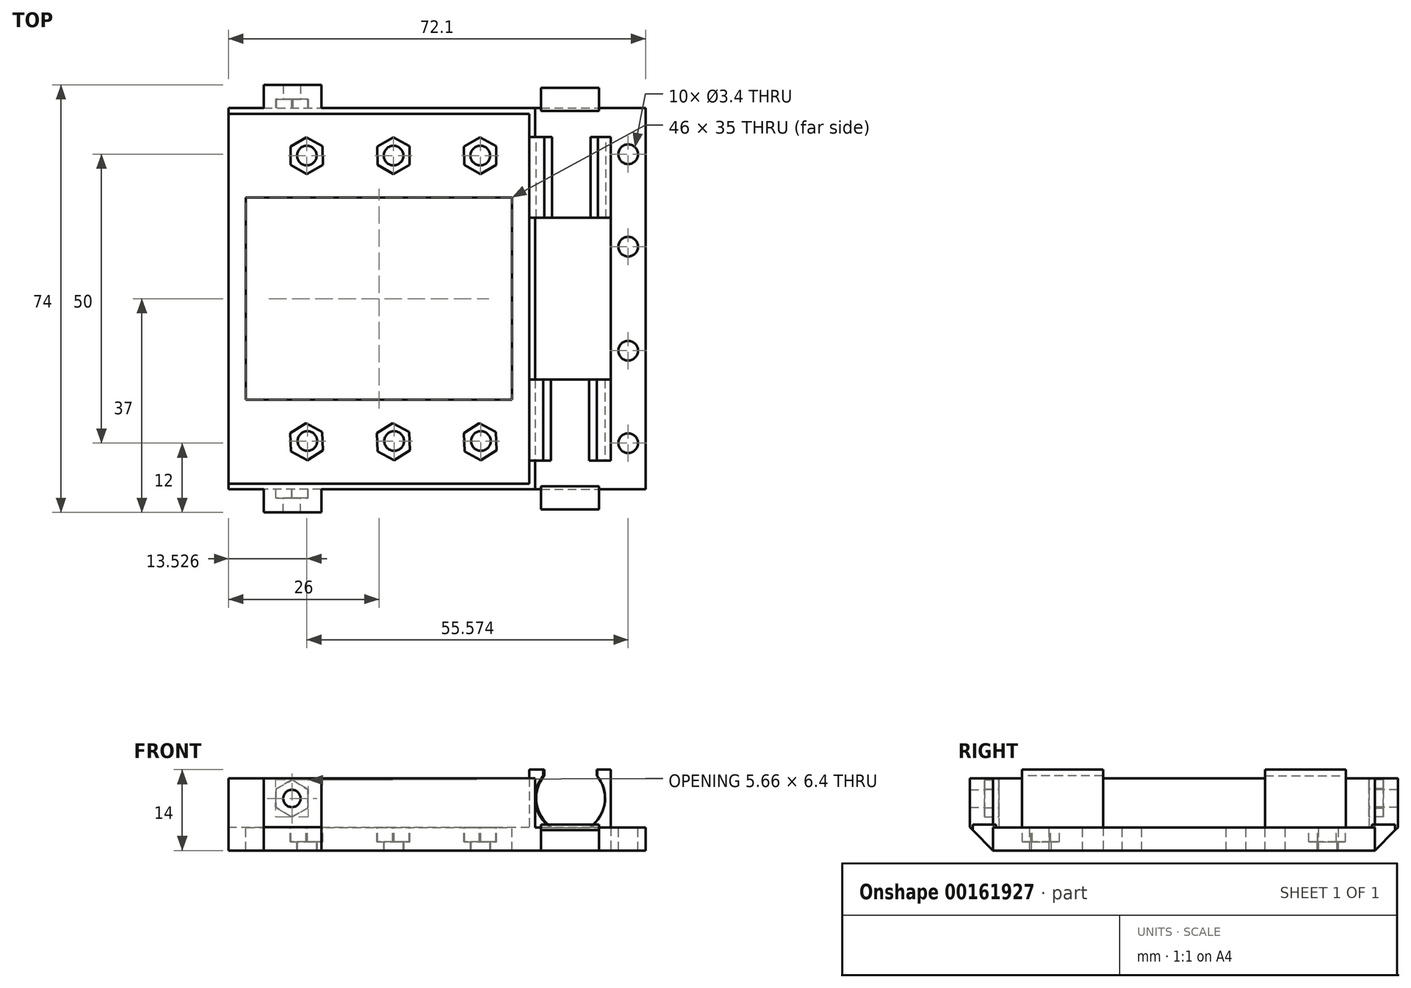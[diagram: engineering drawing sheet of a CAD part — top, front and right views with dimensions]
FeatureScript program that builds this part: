
annotation { "Feature Type Name" : "Feature", "Feature Type Description" : "" }
export const myFeature = defineFeature(function(context is Context, id is Id, definition is map)
    precondition{}
    {
        {
            var Q0;
            Q0=qCreatedBy(makeId("Top.planeOp"),FACE);
            var sketch = newSketch(context, id + "F0", { "sketchPlane" : qUnion([Q0])});
            skLineSegment(sketch, "E0.bottom", {"start": v(-26.5, 33) * mm, "end": v(26.5, 33) * mm});
            skLineSegment(sketch, "E0.top", {"start": v(-26.5, -33) * mm, "end": v(26.5, -33) * mm});
            skLineSegment(sketch, "E0.left", {"start": v(-26.5, 33) * mm, "end": v(-26.5, -33) * mm});
            skLineSegment(sketch, "E0.right", {"start": v(26.5, 33) * mm, "end": v(26.5, -33) * mm});
            skPoint(sketch, "E0.middle", {"position": v(0, 0) * mm});
            skSolve(sketch);
        }
        {
            var Q0;
            Q0 = qSketchRegion(id + "F0", true);
            extrude(context, id + "F1", {"entities" : qUnion([Q0]), "depth" : 12.5 * mm});
        }
        {
            var Q0;
            Q0=makeQuery(id+"F1.opExtrude","SWEPT_FACE",FACE,{"disambiguationData":[OSD([sQuery(id+"F0.wireOp",EDGE,"E0.left")])]});
            var sketch = newSketch(context, id + "F2", { "sketchPlane" : qUnion([Q0])});
            skLineSegment(sketch, "E1.bottom", {"start": v(-32, 12.5) * mm, "end": v(32, 12.5) * mm});
            skLineSegment(sketch, "E1.top", {"start": v(-32, 4) * mm, "end": v(32, 4) * mm});
            skLineSegment(sketch, "E1.left", {"start": v(-32, 12.5) * mm, "end": v(-32, 4) * mm});
            skLineSegment(sketch, "E1.right", {"start": v(32, 12.5) * mm, "end": v(32, 4) * mm});
            skSolve(sketch);
        }
        {
            var Q0;
            Q0 = qSketchRegion(id + "F2", true);
            extrude(context, id + "F3", {"entities" : qUnion([Q0]), "operationType" : NewBodyOperationType.REMOVE, "oppositeDirection" : true, "depth" : 52 * mm});
        }
        {
            var Q0;
            Q0=makeQuery(id+"F3.boolean.opBoolean","COPY",FACE,{"derivedFrom":makeQuery(id+"F3.opExtrude","SWEPT_FACE",FACE,{"disambiguationData":[OSD([sQuery(id+"F2.wireOp",EDGE,"E1.top")])]})});
            var sketch = newSketch(context, id + "F4", { "sketchPlane" : qUnion([Q0])});
            skLineSegment(sketch, "E2.bottom", {"start": v(-23.5, 17.5) * mm, "end": v(22.5, 17.5) * mm});
            skLineSegment(sketch, "E2.top", {"start": v(-23.5, -17.5) * mm, "end": v(22.5, -17.5) * mm});
            skLineSegment(sketch, "E2.left", {"start": v(-23.5, 17.5) * mm, "end": v(-23.5, -17.5) * mm});
            skLineSegment(sketch, "E2.right", {"start": v(22.5, 17.5) * mm, "end": v(22.5, -17.5) * mm});
            skSolve(sketch);
        }
        {
            var Q0;
            Q0 = qSketchRegion(id + "F4", true);
            extrude(context, id + "F5", {"entities" : qUnion([Q0]), "operationType" : NewBodyOperationType.REMOVE, "oppositeDirection" : true, "depth" : 5 * mm});
        }
        {
            var Q0;
            Q0=makeQuery(id+"F1.opExtrude","SWEPT_FACE",FACE,{"disambiguationData":[OSD([sQuery(id+"F0.wireOp",EDGE,"E0.right")])]});
            var sketch = newSketch(context, id + "F6", { "sketchPlane" : qUnion([Q0])});
            skLineSegment(sketch, "E3.bottom", {"start": v(-28, 12.5) * mm, "end": v(-14, 12.5) * mm});
            skLineSegment(sketch, "E3.top", {"start": v(-28, 0) * mm, "end": v(-14, 0) * mm});
            skLineSegment(sketch, "E3.left", {"start": v(-28, 12.5) * mm, "end": v(-28, 0) * mm});
            skLineSegment(sketch, "E3.right", {"start": v(-14, 12.5) * mm, "end": v(-14, 0) * mm});
            skSolve(sketch);
        }
        {
            var Q0;
            Q0 = qSketchRegion(id + "F6", true);
            extrude(context, id + "F7", {"entities" : qUnion([Q0]), "operationType" : NewBodyOperationType.REMOVE, "oppositeDirection" : true, "depth" : 1 * mm});
        }
        {
            var Q0;
            Q0=makeQuery(id+"F7.boolean.opBoolean","COPY",FACE,{"derivedFrom":makeQuery(id+"F7.opExtrude","CAP_FACE",FACE,{"disambiguationData":[OSD([sQuery(id+"F6.wireOp",EDGE,"E3.bottom"),sQuery(id+"F6.wireOp",EDGE,"E3.top"),sQuery(id+"F6.wireOp",EDGE,"E3.left"),sQuery(id+"F6.wireOp",EDGE,"E3.right")])],"isStart":false})});
            var sketch = newSketch(context, id + "F8", { "sketchPlane" : qUnion([Q0])});
            skLineSegment(sketch, "E4.bottom", {"start": v(-14, 0) * mm, "end": v(-28, 0) * mm});
            skLineSegment(sketch, "E4.top", {"start": v(-14, 14) * mm, "end": v(-28, 14) * mm});
            skLineSegment(sketch, "E4.left", {"start": v(-14, 0) * mm, "end": v(-14, 14) * mm});
            skLineSegment(sketch, "E4.right", {"start": v(-28, 0) * mm, "end": v(-28, 14) * mm});
            skSolve(sketch);
        }
        {
            var Q0;
            Q0 = qSketchRegion(id + "F8", true);
            extrude(context, id + "F9", {"entities" : qUnion([Q0]), "operationType" : NewBodyOperationType.ADD, "depth" : 14.1 * mm});
        }
        {
            var Q0;
            Q0=makeQuery(id+"F9.opExtrude","SWEPT_FACE",FACE,{"disambiguationData":[OSD([sQuery(id+"F8.wireOp",EDGE,"E4.right")])]});
            var sketch = newSketch(context, id + "F10", { "sketchPlane" : qUnion([Q0])});
            skArc(sketch, "E5", {"start": v(27.89, 12.91) * mm, "mid": v(26.56, 8.16) * mm, "end": v(29.21, 4) * mm});
            skLineSegment(sketch, "E6", {"start": v(27.89, 14) * mm, "end": v(27.89, 12.91) * mm});
            skLineSegment(sketch, "E7", {"start": v(37.2, 12.91) * mm, "end": v(37.2, 14) * mm});
            skLineSegment(sketch, "E8", {"start": v(27.89, 14) * mm, "end": v(37.2, 14) * mm});
            skLineSegment(sketch, "E9", {"start": v(29.21, 4) * mm, "end": v(35.88, 4) * mm});
            skArc(sketch, "E10.trimOffspring", {"start": v(35.88, 4) * mm, "mid": v(38.53, 8.16) * mm, "end": v(37.2, 12.91) * mm});
            skSolve(sketch);
        }
        {
            var Q0;
            Q0 = qSketchRegion(id + "F10", true);
            extrude(context, id + "F11", {"entities" : qUnion([Q0]), "operationType" : NewBodyOperationType.REMOVE, "oppositeDirection" : true, "depth" : 14 * mm});
        }
        {
            var Q0;
            {var subQ0=sQuery(id+"F0.wireOp",EDGE,"E0.bottom");var subQ1=sQuery(id+"F0.wireOp",EDGE,"E0.right");Q0=makeQuery(id+"F7.boolean.opBoolean","SPLIT",FACE,{"disambiguationData":[TD([makeQuery(id+"F1.opExtrude","SWEPT_FACE",FACE,{"disambiguationData":[OSD([subQ0])]})])],"derivedFrom":makeQuery(id+"F1.opExtrude","SWEPT_FACE",FACE,{"disambiguationData":[OSD([subQ1])]})});}
            var sketch = newSketch(context, id + "F12", { "sketchPlane" : qUnion([Q0])});
            skLineSegment(sketch, "E11.bottom", {"start": v(28, 0) * mm, "end": v(14, 0) * mm});
            skLineSegment(sketch, "E11.top", {"start": v(28, 14) * mm, "end": v(14, 14) * mm});
            skLineSegment(sketch, "E11.left", {"start": v(28, 0) * mm, "end": v(28, 14) * mm});
            skLineSegment(sketch, "E11.right", {"start": v(14, 0) * mm, "end": v(14, 14) * mm});
            skSolve(sketch);
        }
        {
            var Q0;
            Q0 = qSketchRegion(id + "F12", true);
            var Q1;
            {var subQ3=sQuery(id+"F2.wireOp",EDGE,"E1.right");var subQ4=sQuery(id+"F2.wireOp",EDGE,"E1.top");var subQ7=sQuery(id+"F2.wireOp",EDGE,"E1.left");var subQ8=makeQuery(id+"F3.boolean.opBoolean","COPY",FACE,{"derivedFrom":makeQuery(id+"F3.opExtrude","CAP_FACE",FACE,{"disambiguationData":[OSD([sQuery(id+"F2.wireOp",EDGE,"E1.bottom"),subQ4,subQ7,subQ3])],"isStart":false})});Q1=makeQuery(id+"F9.boolean.opBoolean","MERGE",FACE,{"derivedFrom":[makeQuery(id+"F7.boolean.opBoolean","SPLIT",FACE,{"disambiguationData":[TD([makeQuery(id+"F3.boolean.opBoolean","COPY",FACE,{"derivedFrom":makeQuery(id+"F3.opExtrude","SWEPT_FACE",FACE,{"disambiguationData":[OSD([subQ7])]})})])],"derivedFrom":subQ8}),makeQuery(id+"F7.boolean.opBoolean","SPLIT",FACE,{"disambiguationData":[TD([makeQuery(id+"F3.boolean.opBoolean","COPY",FACE,{"derivedFrom":makeQuery(id+"F3.opExtrude","SWEPT_FACE",FACE,{"disambiguationData":[OSD([subQ3])]})})])],"derivedFrom":subQ8}),makeQuery(id+"F9.opExtrude","CAP_FACE",FACE,{"disambiguationData":[OSD([sQuery(id+"F8.wireOp",EDGE,"E4.bottom"),sQuery(id+"F8.wireOp",EDGE,"E4.top"),sQuery(id+"F8.wireOp",EDGE,"E4.left"),sQuery(id+"F8.wireOp",EDGE,"E4.right")])],"isStart":true})]});}
            extrude(context, id + "F13", {"entities" : qUnion([Q0]), "operationType" : NewBodyOperationType.ADD, "endBound" : BoundingType.UP_TO_SURFACE, "oppositeDirection" : true, "endBoundEntityFace" : qUnion([Q1]), "depth" : 25 * mm, "hasSecondDirection" : true, "secondDirectionOppositeDirection" : false, "secondDirectionDepth" : 13.1 * mm});
        }
        {
            var Q0;
            Q0=makeQuery(id+"F13.opExtrude","SWEPT_FACE",FACE,{"disambiguationData":[OSD([sQuery(id+"F12.wireOp",EDGE,"E11.left")])]});
            var sketch = newSketch(context, id + "F14", { "sketchPlane" : qUnion([Q0])});
            skArc(sketch, "E12", {"start": v(-37.37, 12.94) * mm, "mid": v(-38.72, 8.18) * mm, "end": v(-36.07, 4) * mm});
            skLineSegment(sketch, "E13", {"start": v(-36.07, 4) * mm, "end": v(-29.4, 4) * mm});
            skLineSegment(sketch, "E14", {"start": v(-37.37, 14) * mm, "end": v(-37.37, 12.94) * mm});
            skLineSegment(sketch, "E15", {"start": v(-28.1, 12.94) * mm, "end": v(-28.1, 14) * mm});
            skArc(sketch, "E16.trimOffspring", {"start": v(-29.4, 4) * mm, "mid": v(-26.75, 8.18) * mm, "end": v(-28.1, 12.94) * mm});
            skLineSegment(sketch, "E17", {"start": v(-37.37, 14) * mm, "end": v(-28.1, 14) * mm});
            skSolve(sketch);
        }
        {
            var Q0;
            Q0 = qSketchRegion(id + "F14", true);
            extrude(context, id + "F15", {"entities" : qUnion([Q0]), "operationType" : NewBodyOperationType.REMOVE, "oppositeDirection" : true, "depth" : 14 * mm});
        }
        {
            var Q0;
            {var subQ0=sQuery(id+"F0.wireOp",EDGE,"E0.right");var subQ2=sQuery(id+"F0.wireOp",EDGE,"E0.top");Q0=makeQuery(id+"F7.boolean.opBoolean","SPLIT",FACE,{"disambiguationData":[TD([makeQuery(id+"F1.opExtrude","SWEPT_FACE",FACE,{"disambiguationData":[OSD([subQ2])]})])],"derivedFrom":makeQuery(id+"F1.opExtrude","SWEPT_FACE",FACE,{"disambiguationData":[OSD([subQ0])]})});}
            var sketch = newSketch(context, id + "F16", { "sketchPlane" : qUnion([Q0])});
            skLineSegment(sketch, "E18.bottom", {"start": v(-33, 4) * mm, "end": v(-28, 4) * mm});
            skLineSegment(sketch, "E18.top", {"start": v(-33, 0) * mm, "end": v(-28, 0) * mm});
            skLineSegment(sketch, "E18.left", {"start": v(-33, 4) * mm, "end": v(-33, 0) * mm});
            skLineSegment(sketch, "E18.right", {"start": v(-28, 4) * mm, "end": v(-28, 0) * mm});
            skSolve(sketch);
        }
        {
            var Q0;
            Q0 = qSketchRegion(id + "F16", true);
            var Q1;
            Q1=makeQuery(id+"F9.opExtrude","CAP_FACE",FACE,{"disambiguationData":[OSD([sQuery(id+"F8.wireOp",EDGE,"E4.bottom"),sQuery(id+"F8.wireOp",EDGE,"E4.top"),sQuery(id+"F8.wireOp",EDGE,"E4.left"),sQuery(id+"F8.wireOp",EDGE,"E4.right")])],"isStart":false});
            extrude(context, id + "F17", {"entities" : qUnion([Q0]), "operationType" : NewBodyOperationType.ADD, "endBound" : BoundingType.UP_TO_SURFACE, "endBoundEntityFace" : qUnion([Q1]), "depth" : 25 * mm});
        }
        {
            var Q0;
            {var subQ0=sQuery(id+"F0.wireOp",EDGE,"E0.right");var subQ3=sQuery(id+"F0.wireOp",EDGE,"E0.bottom");var subQ6=makeQuery(id+"F1.opExtrude","SWEPT_FACE",FACE,{"disambiguationData":[OSD([subQ3])]});Q0=makeQuery(id+"F13.boolean.opBoolean","SPLIT",FACE,{"disambiguationData":[TD([subQ6])],"derivedFrom":makeQuery(id+"F7.boolean.opBoolean","SPLIT",FACE,{"disambiguationData":[TD([subQ6])],"derivedFrom":makeQuery(id+"F1.opExtrude","SWEPT_FACE",FACE,{"disambiguationData":[OSD([subQ0])]})})});}
            var sketch = newSketch(context, id + "F18", { "sketchPlane" : qUnion([Q0])});
            skLineSegment(sketch, "E19.bottom", {"start": v(28, 4) * mm, "end": v(33, 4) * mm});
            skLineSegment(sketch, "E19.top", {"start": v(28, 0) * mm, "end": v(33, 0) * mm});
            skLineSegment(sketch, "E19.left", {"start": v(28, 4) * mm, "end": v(28, 0) * mm});
            skLineSegment(sketch, "E19.right", {"start": v(33, 4) * mm, "end": v(33, 0) * mm});
            skSolve(sketch);
        }
        {
            var Q0;
            Q0 = qSketchRegion(id + "F18", true);
            var Q1;
            Q1=makeQuery(id+"F13.opExtrude","CAP_FACE",FACE,{"disambiguationData":[OSD([sQuery(id+"F12.wireOp",EDGE,"E11.bottom"),sQuery(id+"F12.wireOp",EDGE,"E11.top"),sQuery(id+"F12.wireOp",EDGE,"E11.left"),sQuery(id+"F12.wireOp",EDGE,"E11.right")])],"isStart":true});
            extrude(context, id + "F19", {"entities" : qUnion([Q0]), "operationType" : NewBodyOperationType.ADD, "endBound" : BoundingType.UP_TO_SURFACE, "endBoundEntityFace" : qUnion([Q1]), "depth" : 25 * mm});
        }
        {
            var Q0;
            {var subQ0=sQuery(id+"F8.wireOp",EDGE,"E4.right");var subQ1=sQuery(id+"F8.wireOp",EDGE,"E4.left");var subQ2=sQuery(id+"F8.wireOp",EDGE,"E4.top");var subQ3=sQuery(id+"F8.wireOp",EDGE,"E4.bottom");Q0=makeQuery(id+"F17.boolean.opBoolean","MERGE",FACE,{"derivedFrom":[makeQuery(id+"F9.opExtrude","CAP_FACE",FACE,{"disambiguationData":[OSD([subQ3,subQ2,subQ1,subQ0])],"isStart":false}),makeQuery(id+"F17.opExtrude","CAP_FACE",FACE,{"disambiguationData":[OSD([subQ3,subQ2,subQ1,subQ0])],"isStart":false})]});}
            var sketch = newSketch(context, id + "F20", { "sketchPlane" : qUnion([Q0])});
            skLineSegment(sketch, "E20.bottom", {"start": v(-33, 4) * mm, "end": v(33, 4) * mm});
            skLineSegment(sketch, "E20.top", {"start": v(-33, 0) * mm, "end": v(33, 0) * mm});
            skLineSegment(sketch, "E20.left", {"start": v(-33, 4) * mm, "end": v(-33, 0) * mm});
            skLineSegment(sketch, "E20.right", {"start": v(33, 4) * mm, "end": v(33, 0) * mm});
            skSolve(sketch);
        }
        {
            var Q0;
            Q0 = qSketchRegion(id + "F20", true);
            extrude(context, id + "F21", {"entities" : qUnion([Q0]), "operationType" : NewBodyOperationType.ADD, "depth" : 6 * mm});
        }
        {
            var Q0;
            Q0=makeQuery(id+"F21.boolean.opBoolean","MERGE",FACE,{"derivedFrom":[makeQuery(id+"F17.boolean.opBoolean","MERGE",FACE,{"derivedFrom":[makeQuery(id+"F1.opExtrude","SWEPT_FACE",FACE,{"disambiguationData":[OSD([sQuery(id+"F0.wireOp",EDGE,"E0.top")])]}),makeQuery(id+"F17.opExtrude","SWEPT_FACE",FACE,{"disambiguationData":[OSD([sQuery(id+"F16.wireOp",EDGE,"E18.left")])]})]}),makeQuery(id+"F21.opExtrude","SWEPT_FACE",FACE,{"disambiguationData":[OSD([sQuery(id+"F20.wireOp",EDGE,"E20.left")])]})]});
            var sketch = newSketch(context, id + "F22", { "sketchPlane" : qUnion([Q0])});
            skLineSegment(sketch, "E21.bottom", {"start": v(37.55, 0) * mm, "end": v(27.55, 0) * mm});
            skLineSegment(sketch, "E21.top", {"start": v(37.55, 4.5) * mm, "end": v(27.55, 4.5) * mm});
            skLineSegment(sketch, "E21.left", {"start": v(37.55, 0) * mm, "end": v(37.55, 4.5) * mm});
            skLineSegment(sketch, "E21.right", {"start": v(27.55, 0) * mm, "end": v(27.55, 4.5) * mm});
            skSolve(sketch);
        }
        {
            var Q0;
            Q0 = qSketchRegion(id + "F22", true);
            extrude(context, id + "F23", {"entities" : qUnion([Q0]), "operationType" : NewBodyOperationType.ADD, "oppositeDirection" : true, "depth" : .5 * mm, "hasSecondDirection" : true, "secondDirectionOppositeDirection" : false, "secondDirectionDepth" : 3.5 * mm});
        }
        {
            var Q0;
            Q0=makeQuery(id+"F23.opExtrude","SWEPT_FACE",FACE,{"disambiguationData":[OSD([sQuery(id+"F22.wireOp",EDGE,"E21.left")])]});
            var sketch = newSketch(context, id + "F24", { "sketchPlane" : qUnion([Q0])});
            skLineSegment(sketch, "E22", {"start": v(-33, 0) * mm, "end": v(-36.5, 3.5) * mm});
            skLineSegment(sketch, "E23", {"start": v(-36.5, 3.5) * mm, "end": v(-36.5, 0) * mm});
            skLineSegment(sketch, "E24", {"start": v(-36.5, 0) * mm, "end": v(-33, 0) * mm});
            skSolve(sketch);
        }
        {
            var Q0;
            Q0 = qSketchRegion(id + "F24", true);
            extrude(context, id + "F25", {"entities" : qUnion([Q0]), "operationType" : NewBodyOperationType.REMOVE, "oppositeDirection" : true, "depth" : 10 * mm});
        }
        {
            var Q0;
            {var subQ1=sQuery(id+"F0.wireOp",EDGE,"E0.left");var subQ2=sQuery(id+"F0.wireOp",EDGE,"E0.top");Q0=makeQuery(id+"F23.boolean.opBoolean","SPLIT",FACE,{"disambiguationData":[TD([makeQuery(id+"F1.opExtrude","SWEPT_FACE",FACE,{"disambiguationData":[OSD([subQ1])]})])],"derivedFrom":makeQuery(id+"F21.boolean.opBoolean","MERGE",FACE,{"derivedFrom":[makeQuery(id+"F17.boolean.opBoolean","MERGE",FACE,{"derivedFrom":[makeQuery(id+"F1.opExtrude","SWEPT_FACE",FACE,{"disambiguationData":[OSD([subQ2])]}),makeQuery(id+"F17.opExtrude","SWEPT_FACE",FACE,{"disambiguationData":[OSD([sQuery(id+"F16.wireOp",EDGE,"E18.left")])]})]}),makeQuery(id+"F21.opExtrude","SWEPT_FACE",FACE,{"disambiguationData":[OSD([sQuery(id+"F20.wireOp",EDGE,"E20.left")])]})]})});}
            var sketch = newSketch(context, id + "F26", { "sketchPlane" : qUnion([Q0])});
            skLineSegment(sketch, "E25.bottom", {"start": v(-20.45, 12.5) * mm, "end": v(-10.45, 12.5) * mm});
            skLineSegment(sketch, "E25.top", {"start": v(-20.45, 0) * mm, "end": v(-10.45, 0) * mm});
            skLineSegment(sketch, "E25.left", {"start": v(-20.45, 12.5) * mm, "end": v(-20.45, 0) * mm});
            skLineSegment(sketch, "E25.right", {"start": v(-10.45, 12.5) * mm, "end": v(-10.45, 0) * mm});
            skSolve(sketch);
        }
        {
            var Q0;
            Q0 = qSketchRegion(id + "F26", true);
            extrude(context, id + "F27", {"entities" : qUnion([Q0]), "operationType" : NewBodyOperationType.ADD, "depth" : 4 * mm});
        }
        {
            var Q0;
            Q0=makeQuery(id+"F27.opExtrude","SWEPT_FACE",FACE,{"disambiguationData":[OSD([sQuery(id+"F26.wireOp",EDGE,"E25.left")])]});
            var sketch = newSketch(context, id + "F28", { "sketchPlane" : qUnion([Q0])});
            skLineSegment(sketch, "E26", {"start": v(37, 0) * mm, "end": v(37, 4.04) * mm});
            skLineSegment(sketch, "E27", {"start": v(37, 4.04) * mm, "end": v(33, 0) * mm});
            skLineSegment(sketch, "E28", {"start": v(33, 0) * mm, "end": v(37, 0) * mm});
            skSolve(sketch);
        }
        {
            var Q0;
            Q0 = qSketchRegion(id + "F28", true);
            var Q1;
            Q1=makeQuery(id+"F27.opExtrude","SWEPT_FACE",FACE,{"disambiguationData":[OSD([sQuery(id+"F26.wireOp",EDGE,"E25.right")])]});
            extrude(context, id + "F29", {"entities" : qUnion([Q0]), "operationType" : NewBodyOperationType.REMOVE, "endBound" : BoundingType.UP_TO_SURFACE, "oppositeDirection" : true, "endBoundEntityFace" : qUnion([Q1]), "depth" : 25 * mm});
        }
        {
            var Q0;
            Q0=makeQuery(id+"F21.boolean.opBoolean","MERGE",FACE,{"derivedFrom":[makeQuery(id+"F19.boolean.opBoolean","MERGE",FACE,{"derivedFrom":[makeQuery(id+"F1.opExtrude","SWEPT_FACE",FACE,{"disambiguationData":[OSD([sQuery(id+"F0.wireOp",EDGE,"E0.bottom")])]}),makeQuery(id+"F19.opExtrude","SWEPT_FACE",FACE,{"disambiguationData":[OSD([sQuery(id+"F18.wireOp",EDGE,"E19.right")])]})]}),makeQuery(id+"F21.opExtrude","SWEPT_FACE",FACE,{"disambiguationData":[OSD([sQuery(id+"F20.wireOp",EDGE,"E20.right")])]})]});
            var sketch = newSketch(context, id + "F30", { "sketchPlane" : qUnion([Q0])});
            skLineSegment(sketch, "E29.bottom", {"start": v(-27.55, 0) * mm, "end": v(-37.55, 0) * mm});
            skLineSegment(sketch, "E29.top", {"start": v(-27.55, 4.5) * mm, "end": v(-37.55, 4.5) * mm});
            skLineSegment(sketch, "E29.left", {"start": v(-27.55, 0) * mm, "end": v(-27.55, 4.5) * mm});
            skLineSegment(sketch, "E29.right", {"start": v(-37.55, 0) * mm, "end": v(-37.55, 4.5) * mm});
            skSolve(sketch);
        }
        {
            var Q0;
            Q0 = qSketchRegion(id + "F30", true);
            extrude(context, id + "F31", {"entities" : qUnion([Q0]), "operationType" : NewBodyOperationType.ADD, "oppositeDirection" : true, "depth" : 0.5 * mm, "hasSecondDirection" : true, "secondDirectionOppositeDirection" : false, "secondDirectionDepth" : 3.5 * mm});
        }
        {
            var Q0;
            Q0=makeQuery(id+"F31.opExtrude","SWEPT_FACE",FACE,{"disambiguationData":[OSD([sQuery(id+"F30.wireOp",EDGE,"E29.right")])]});
            var sketch = newSketch(context, id + "F32", { "sketchPlane" : qUnion([Q0])});
            skLineSegment(sketch, "E30", {"start": v(33, 0) * mm, "end": v(36.5, 3.5) * mm});
            skLineSegment(sketch, "E31", {"start": v(36.5, 3.5) * mm, "end": v(36.5, 0) * mm});
            skLineSegment(sketch, "E32", {"start": v(36.5, 0) * mm, "end": v(33, 0) * mm});
            skSolve(sketch);
        }
        {
            var Q0;
            Q0 = qSketchRegion(id + "F32", true);
            var Q1;
            Q1=makeQuery(id+"F31.opExtrude","SWEPT_FACE",FACE,{"disambiguationData":[OSD([sQuery(id+"F30.wireOp",EDGE,"E29.left")])]});
            extrude(context, id + "F33", {"entities" : qUnion([Q0]), "operationType" : NewBodyOperationType.REMOVE, "endBound" : BoundingType.UP_TO_SURFACE, "oppositeDirection" : true, "endBoundEntityFace" : qUnion([Q1]), "depth" : 25 * mm});
        }
        {
            var Q0;
            {var subQ1=sQuery(id+"F0.wireOp",EDGE,"E0.left");var subQ3=sQuery(id+"F0.wireOp",EDGE,"E0.bottom");Q0=makeQuery(id+"F31.boolean.opBoolean","SPLIT",FACE,{"disambiguationData":[TD([makeQuery(id+"F1.opExtrude","SWEPT_FACE",FACE,{"disambiguationData":[OSD([subQ1])]})])],"derivedFrom":makeQuery(id+"F21.boolean.opBoolean","MERGE",FACE,{"derivedFrom":[makeQuery(id+"F19.boolean.opBoolean","MERGE",FACE,{"derivedFrom":[makeQuery(id+"F1.opExtrude","SWEPT_FACE",FACE,{"disambiguationData":[OSD([subQ3])]}),makeQuery(id+"F19.opExtrude","SWEPT_FACE",FACE,{"disambiguationData":[OSD([sQuery(id+"F18.wireOp",EDGE,"E19.right")])]})]}),makeQuery(id+"F21.opExtrude","SWEPT_FACE",FACE,{"disambiguationData":[OSD([sQuery(id+"F20.wireOp",EDGE,"E20.right")])]})]})});}
            var sketch = newSketch(context, id + "F34", { "sketchPlane" : qUnion([Q0])});
            skLineSegment(sketch, "E33.bottom", {"start": v(10.45, 12.5) * mm, "end": v(20.45, 12.5) * mm});
            skLineSegment(sketch, "E33.top", {"start": v(10.45, 0) * mm, "end": v(20.45, 0) * mm});
            skLineSegment(sketch, "E33.left", {"start": v(10.45, 12.5) * mm, "end": v(10.45, 0) * mm});
            skLineSegment(sketch, "E33.right", {"start": v(20.45, 12.5) * mm, "end": v(20.45, 0) * mm});
            skSolve(sketch);
        }
        {
            var Q0;
            Q0 = qSketchRegion(id + "F34", true);
            extrude(context, id + "F35", {"entities" : qUnion([Q0]), "operationType" : NewBodyOperationType.ADD, "depth" : 4 * mm});
        }
        {
            var Q0;
            Q0=makeQuery(id+"F35.opExtrude","SWEPT_FACE",FACE,{"disambiguationData":[OSD([sQuery(id+"F34.wireOp",EDGE,"E33.left")])]});
            var sketch = newSketch(context, id + "F36", { "sketchPlane" : qUnion([Q0])});
            skLineSegment(sketch, "E34", {"start": v(33, 0) * mm, "end": v(37, 4) * mm});
            skLineSegment(sketch, "E35", {"start": v(37, 4) * mm, "end": v(37, 0) * mm});
            skLineSegment(sketch, "E36", {"start": v(37, 0) * mm, "end": v(33, 0) * mm});
            skSolve(sketch);
        }
        {
            var Q0;
            Q0 = qSketchRegion(id + "F36", true);
            var Q1;
            Q1=makeQuery(id+"F35.opExtrude","SWEPT_FACE",FACE,{"disambiguationData":[OSD([sQuery(id+"F34.wireOp",EDGE,"E33.right")])]});
            extrude(context, id + "F37", {"entities" : qUnion([Q0]), "operationType" : NewBodyOperationType.REMOVE, "endBound" : BoundingType.UP_TO_SURFACE, "oppositeDirection" : true, "endBoundEntityFace" : qUnion([Q1]), "depth" : 25 * mm});
        }
        {
            var Q0;
            Q0=makeQuery(id+"F3.boolean.opBoolean","COPY",FACE,{"derivedFrom":makeQuery(id+"F3.opExtrude","SWEPT_FACE",FACE,{"disambiguationData":[OSD([sQuery(id+"F2.wireOp",EDGE,"E1.right")])]})});
            var sketch = newSketch(context, id + "F38", { "sketchPlane" : qUnion([Q0])});
            skCircle(sketch, "E37.cCircle", {"center": v(15.55, 9) * mm, "radius": 2.77 * mm, "construction": true});
            skLineSegment(sketch, "E37.0", {"start": v(12.8, 10.62) * mm, "end": v(15.57, 12.2) * mm});
            skLineSegment(sketch, "E37.1", {"start": v(15.57, 12.2) * mm, "end": v(18.33, 10.58) * mm});
            skLineSegment(sketch, "E37.2", {"start": v(18.33, 10.58) * mm, "end": v(18.3, 7.38) * mm});
            skLineSegment(sketch, "E37.3", {"start": v(18.3, 7.38) * mm, "end": v(15.53, 5.8) * mm});
            skLineSegment(sketch, "E37.4", {"start": v(15.53, 5.8) * mm, "end": v(12.77, 7.42) * mm});
            skLineSegment(sketch, "E37.5", {"start": v(12.77, 7.42) * mm, "end": v(12.8, 10.62) * mm});
            skPoint(sketch, "E37.0.midPoint", {"position": v(14.18, 11.41) * mm});
            skSolve(sketch);
        }
        {
            var Q0;
            Q0 = qSketchRegion(id + "F38", true);
            extrude(context, id + "F39", {"entities" : qUnion([Q0]), "operationType" : NewBodyOperationType.REMOVE, "oppositeDirection" : true, "depth" : 2.5 * mm});
        }
        {
            var Q0;
            Q0=makeQuery(id+"F3.boolean.opBoolean","COPY",FACE,{"derivedFrom":makeQuery(id+"F3.opExtrude","SWEPT_FACE",FACE,{"disambiguationData":[OSD([sQuery(id+"F2.wireOp",EDGE,"E1.right")])]})});
            var sketch = newSketch(context, id + "F40", { "sketchPlane" : qUnion([Q0])});
            skCircle(sketch, "E38", {"center": v(15.55, 9) * mm, "radius": 1.5 * mm});
            skSolve(sketch);
        }
        {
            var Q0;
            Q0 = qSketchRegion(id + "F40", true);
            extrude(context, id + "F41", {"entities" : qUnion([Q0]), "operationType" : NewBodyOperationType.REMOVE, "oppositeDirection" : true, "depth" : 6 * mm});
        }
        {
            var Q0;
            Q0=makeQuery(id+"F3.boolean.opBoolean","COPY",FACE,{"derivedFrom":makeQuery(id+"F3.opExtrude","SWEPT_FACE",FACE,{"disambiguationData":[OSD([sQuery(id+"F2.wireOp",EDGE,"E1.left")])]})});
            var sketch = newSketch(context, id + "F42", { "sketchPlane" : qUnion([Q0])});
            skCircle(sketch, "E39.cCircle", {"center": v(-15.55, 9) * mm, "radius": 2.77 * mm, "construction": true});
            skLineSegment(sketch, "E39.0", {"start": v(-12.84, 7.3) * mm, "end": v(-15.67, 5.8) * mm});
            skLineSegment(sketch, "E39.1", {"start": v(-15.67, 5.8) * mm, "end": v(-18.38, 7.5) * mm});
            skLineSegment(sketch, "E39.2", {"start": v(-18.38, 7.5) * mm, "end": v(-18.26, 10.7) * mm});
            skLineSegment(sketch, "E39.3", {"start": v(-18.26, 10.7) * mm, "end": v(-15.43, 12.2) * mm});
            skLineSegment(sketch, "E39.4", {"start": v(-15.43, 12.2) * mm, "end": v(-12.72, 10.5) * mm});
            skLineSegment(sketch, "E39.5", {"start": v(-12.72, 10.5) * mm, "end": v(-12.84, 7.3) * mm});
            skPoint(sketch, "E39.0.midPoint", {"position": v(-14.25, 6.55) * mm});
            skSolve(sketch);
        }
        {
            var Q0;
            Q0 = qSketchRegion(id + "F42", true);
            extrude(context, id + "F43", {"entities" : qUnion([Q0]), "operationType" : NewBodyOperationType.REMOVE, "oppositeDirection" : true, "depth" : 2.5 * mm});
        }
        {
            var Q0;
            Q0=makeQuery(id+"F3.boolean.opBoolean","COPY",FACE,{"derivedFrom":makeQuery(id+"F3.opExtrude","SWEPT_FACE",FACE,{"disambiguationData":[OSD([sQuery(id+"F2.wireOp",EDGE,"E1.left")])]})});
            var sketch = newSketch(context, id + "F44", { "sketchPlane" : qUnion([Q0])});
            skCircle(sketch, "E40", {"center": v(-15.55, 9) * mm, "radius": 1.5 * mm});
            skSolve(sketch);
        }
        {
            var Q0;
            Q0 = qSketchRegion(id + "F44", true);
            extrude(context, id + "F45", {"entities" : qUnion([Q0]), "operationType" : NewBodyOperationType.REMOVE, "oppositeDirection" : true, "depth" : 6 * mm});
        }
        {
            var Q0;
            Q0=makeQuery(id+"F21.boolean.opBoolean","MERGE",FACE,{"derivedFrom":[makeQuery(id+"F17.boolean.opBoolean","MERGE",FACE,{"derivedFrom":[makeQuery(id+"F11.boolean.opBoolean","COPY",FACE,{"derivedFrom":makeQuery(id+"F11.opExtrude","SWEPT_FACE",FACE,{"disambiguationData":[OSD([sQuery(id+"F10.wireOp",EDGE,"E9")])]})}),makeQuery(id+"F17.opExtrude","SWEPT_FACE",FACE,{"disambiguationData":[OSD([sQuery(id+"F16.wireOp",EDGE,"E18.bottom")])]})]}),makeQuery(id+"F19.boolean.opBoolean","MERGE",FACE,{"derivedFrom":[makeQuery(id+"F15.boolean.opBoolean","COPY",FACE,{"derivedFrom":makeQuery(id+"F15.opExtrude","SWEPT_FACE",FACE,{"disambiguationData":[OSD([sQuery(id+"F14.wireOp",EDGE,"E13")])]})}),makeQuery(id+"F19.opExtrude","SWEPT_FACE",FACE,{"disambiguationData":[OSD([sQuery(id+"F18.wireOp",EDGE,"E19.bottom")])]})]}),makeQuery(id+"F21.opExtrude","SWEPT_FACE",FACE,{"disambiguationData":[OSD([sQuery(id+"F20.wireOp",EDGE,"E20.bottom")])]})]});
            var sketch = newSketch(context, id + "F46", { "sketchPlane" : qUnion([Q0])});
            skCircle(sketch, "E41", {"center": v(42.6, -25) * mm, "radius": 1.7 * mm});
            skCircle(sketch, "E42", {"center": v(42.6, -9) * mm, "radius": 1.7 * mm});
            skCircle(sketch, "E43", {"center": v(42.6, 9) * mm, "radius": 1.7 * mm});
            skCircle(sketch, "E44", {"center": v(42.6, 25) * mm, "radius": 1.7 * mm});
            skSolve(sketch);
        }
        {
            var Q0;
            Q0 = qSketchRegion(id + "F46", true);
            extrude(context, id + "F47", {"entities" : qUnion([Q0]), "operationType" : NewBodyOperationType.REMOVE, "oppositeDirection" : true, "depth" : 5 * mm});
        }
        {
            var Q0;
            Q0=makeQuery(id+"F3.boolean.opBoolean","COPY",FACE,{"derivedFrom":makeQuery(id+"F3.opExtrude","SWEPT_FACE",FACE,{"disambiguationData":[OSD([sQuery(id+"F2.wireOp",EDGE,"E1.top")])]})});
            var sketch = newSketch(context, id + "F48", { "sketchPlane" : qUnion([Q0])});
            skCircle(sketch, "E45.cCircle", {"center": v(-13, 24.75) * mm, "radius": 2.77 * mm, "construction": true});
            skLineSegment(sketch, "E45.0", {"start": v(-10.22, 23.17) * mm, "end": v(-12.97, 21.55) * mm});
            skLineSegment(sketch, "E45.1", {"start": v(-12.97, 21.55) * mm, "end": v(-15.76, 23.13) * mm});
            skLineSegment(sketch, "E45.2", {"start": v(-15.76, 23.13) * mm, "end": v(-15.78, 26.33) * mm});
            skLineSegment(sketch, "E45.3", {"start": v(-15.78, 26.33) * mm, "end": v(-13.03, 27.95) * mm});
            skLineSegment(sketch, "E45.4", {"start": v(-13.03, 27.95) * mm, "end": v(-10.24, 26.37) * mm});
            skLineSegment(sketch, "E45.5", {"start": v(-10.24, 26.37) * mm, "end": v(-10.22, 23.17) * mm});
            skPoint(sketch, "E45.0.midPoint", {"position": v(-11.6, 22.36) * mm});
            skCircle(sketch, "E46.cCircle", {"center": v(2, 24.75) * mm, "radius": 2.77 * mm, "construction": true});
            skLineSegment(sketch, "E46.0", {"start": v(4.78, 23.17) * mm, "end": v(2.03, 21.55) * mm});
            skLineSegment(sketch, "E46.1", {"start": v(2.03, 21.55) * mm, "end": v(-0.76, 23.13) * mm});
            skLineSegment(sketch, "E46.2", {"start": v(-0.76, 23.13) * mm, "end": v(-0.78, 26.33) * mm});
            skLineSegment(sketch, "E46.3", {"start": v(-0.78, 26.33) * mm, "end": v(1.97, 27.95) * mm});
            skLineSegment(sketch, "E46.4", {"start": v(1.97, 27.95) * mm, "end": v(4.76, 26.37) * mm});
            skLineSegment(sketch, "E46.5", {"start": v(4.76, 26.37) * mm, "end": v(4.78, 23.17) * mm});
            skPoint(sketch, "E46.0.midPoint", {"position": v(3.4, 22.36) * mm});
            skCircle(sketch, "E47.cCircle", {"center": v(17, 24.75) * mm, "radius": 2.77 * mm, "construction": true});
            skLineSegment(sketch, "E47.0", {"start": v(19.78, 23.17) * mm, "end": v(17.03, 21.55) * mm});
            skLineSegment(sketch, "E47.1", {"start": v(17.03, 21.55) * mm, "end": v(14.24, 23.13) * mm});
            skLineSegment(sketch, "E47.2", {"start": v(14.24, 23.13) * mm, "end": v(14.22, 26.33) * mm});
            skLineSegment(sketch, "E47.3", {"start": v(14.22, 26.33) * mm, "end": v(16.97, 27.95) * mm});
            skLineSegment(sketch, "E47.4", {"start": v(16.97, 27.95) * mm, "end": v(19.76, 26.37) * mm});
            skLineSegment(sketch, "E47.5", {"start": v(19.76, 26.37) * mm, "end": v(19.78, 23.17) * mm});
            skPoint(sketch, "E47.0.midPoint", {"position": v(18.4, 22.36) * mm});
            skCircle(sketch, "E48.cCircle", {"center": v(-13, -24.75) * mm, "radius": 2.77 * mm, "construction": true});
            skLineSegment(sketch, "E48.0", {"start": v(-10.17, -26.24) * mm, "end": v(-12.87, -27.95) * mm});
            skLineSegment(sketch, "E48.1", {"start": v(-12.87, -27.95) * mm, "end": v(-15.7, -26.46) * mm});
            skLineSegment(sketch, "E48.2", {"start": v(-15.7, -26.46) * mm, "end": v(-15.83, -23.26) * mm});
            skLineSegment(sketch, "E48.3", {"start": v(-15.83, -23.26) * mm, "end": v(-13.13, -21.55) * mm});
            skLineSegment(sketch, "E48.4", {"start": v(-13.13, -21.55) * mm, "end": v(-10.3, -23.04) * mm});
            skLineSegment(sketch, "E48.5", {"start": v(-10.3, -23.04) * mm, "end": v(-10.17, -26.24) * mm});
            skPoint(sketch, "E48.0.midPoint", {"position": v(-11.52, -27.1) * mm});
            skCircle(sketch, "E49.cCircle", {"center": v(2, -24.75) * mm, "radius": 2.77 * mm, "construction": true});
            skLineSegment(sketch, "E49.0", {"start": v(4.83, -26.24) * mm, "end": v(2.13, -27.95) * mm});
            skLineSegment(sketch, "E49.1", {"start": v(2.13, -27.95) * mm, "end": v(-0.7, -26.46) * mm});
            skLineSegment(sketch, "E49.2", {"start": v(-0.7, -26.46) * mm, "end": v(-0.83, -23.26) * mm});
            skLineSegment(sketch, "E49.3", {"start": v(-0.83, -23.26) * mm, "end": v(1.87, -21.55) * mm});
            skLineSegment(sketch, "E49.4", {"start": v(1.87, -21.55) * mm, "end": v(4.7, -23.04) * mm});
            skLineSegment(sketch, "E49.5", {"start": v(4.7, -23.04) * mm, "end": v(4.83, -26.24) * mm});
            skPoint(sketch, "E49.0.midPoint", {"position": v(3.48, -27.1) * mm});
            skCircle(sketch, "E50.cCircle", {"center": v(17, -24.75) * mm, "radius": 2.77 * mm, "construction": true});
            skLineSegment(sketch, "E50.0", {"start": v(19.83, -26.24) * mm, "end": v(17.13, -27.95) * mm});
            skLineSegment(sketch, "E50.1", {"start": v(17.13, -27.95) * mm, "end": v(14.3, -26.46) * mm});
            skLineSegment(sketch, "E50.2", {"start": v(14.3, -26.46) * mm, "end": v(14.17, -23.26) * mm});
            skLineSegment(sketch, "E50.3", {"start": v(14.17, -23.26) * mm, "end": v(16.87, -21.55) * mm});
            skLineSegment(sketch, "E50.4", {"start": v(16.87, -21.55) * mm, "end": v(19.7, -23.04) * mm});
            skLineSegment(sketch, "E50.5", {"start": v(19.7, -23.04) * mm, "end": v(19.83, -26.24) * mm});
            skPoint(sketch, "E50.0.midPoint", {"position": v(18.48, -27.1) * mm});
            skSolve(sketch);
        }
        {
            var Q0;
            Q0 = qSketchRegion(id + "F48", true);
            extrude(context, id + "F49", {"entities" : qUnion([Q0]), "operationType" : NewBodyOperationType.REMOVE, "oppositeDirection" : true, "depth" : 2.5 * mm});
        }
        {
            var Q0;
            Q0=makeQuery(id+"F3.boolean.opBoolean","COPY",FACE,{"derivedFrom":makeQuery(id+"F3.opExtrude","SWEPT_FACE",FACE,{"disambiguationData":[OSD([sQuery(id+"F2.wireOp",EDGE,"E1.top")])]})});
            var sketch = newSketch(context, id + "F50", { "sketchPlane" : qUnion([Q0])});
            skCircle(sketch, "E51", {"center": v(-12.97, 24.77) * mm, "radius": 1.7 * mm});
            skPoint(sketch, "E51.centerSnap0", {"position": v(-10.23, 24.77) * mm});
            skPoint(sketch, "E51.perimeterSnap0", {"position": v(-14.4, 27.14) * mm});
            skPoint(sketch, "E51.perimeterSnap1", {"position": v(-10.23, 24.77) * mm});
            skCircle(sketch, "E52", {"center": v(2.03, 24.77) * mm, "radius": 1.7 * mm});
            skPoint(sketch, "E52.centerSnap0", {"position": v(4.77, 24.77) * mm});
            skCircle(sketch, "E53", {"center": v(17.03, 24.77) * mm, "radius": 1.7 * mm});
            skPoint(sketch, "E53.centerSnap0", {"position": v(19.77, 24.77) * mm});
            skPoint(sketch, "E53.perimeterSnap0", {"position": v(19.77, 24.77) * mm});
            skPoint(sketch, "E53.perimeterSnap1", {"position": v(15.63, 22.34) * mm});
            skCircle(sketch, "E54", {"center": v(17.13, -24.64) * mm, "radius": 1.7 * mm});
            skPoint(sketch, "E54.centerSnap0", {"position": v(19.77, -24.64) * mm});
            skCircle(sketch, "E55", {"center": v(2.13, -24.64) * mm, "radius": 1.7 * mm});
            skPoint(sketch, "E55.centerSnap0", {"position": v(4.77, -24.64) * mm});
            skCircle(sketch, "E56", {"center": v(-12.87, -24.64) * mm, "radius": 1.7 * mm});
            skPoint(sketch, "E56.centerSnap0", {"position": v(-10.23, -24.64) * mm});
            skSolve(sketch);
        }
        {
            var Q0;
            Q0 = qSketchRegion(id + "F50", true);
            extrude(context, id + "F51", {"entities" : qUnion([Q0]), "operationType" : NewBodyOperationType.REMOVE, "oppositeDirection" : true, "depth" : 6 * mm});
        }
    });
